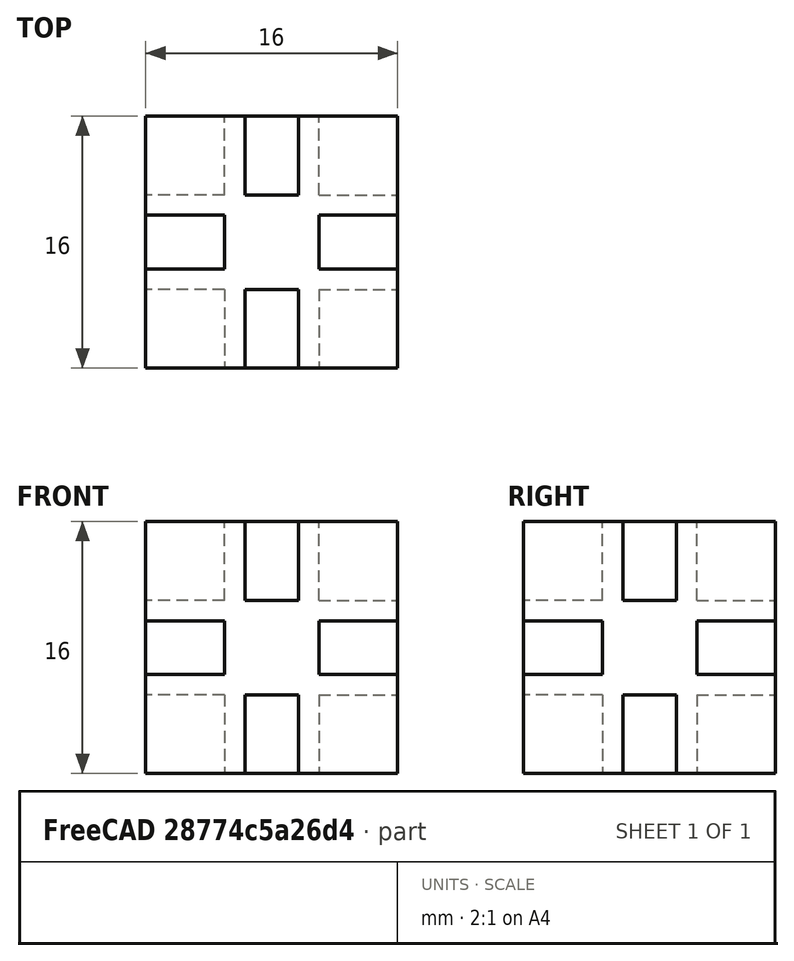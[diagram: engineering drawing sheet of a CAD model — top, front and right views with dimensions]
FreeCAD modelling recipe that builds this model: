
FCSTD DOCUMENT  (FreeCAD 0.14R3702 (Git))
Label: estanteria_disquette2
License: CC-BY 3.0
LicenseURL: http://creativecommons.org/licenses/by/3.0/
objects: Part::Box×2, Part::FeaturePython×2, Part::Cut×1
note: 5 computed .brp shape members not serialized (recipe doc carries the construction recipe); baked Part::Feature solids carry a one-line shape summary decoded from their .brp

FEATURE [Part::Box] Box002  label="Cubo002"
  Height = 3.4
  Length = 90
  Placement = pos=(3,3,-1.7) rot=(0,0,1;0rad)
  Width = 90
FEATURE [Part::FeaturePython] Array004  # Draft array (typed FeaturePython)
  Angle = 180
  ArrayType = 1
  Axis = (0,1,0)
  Base = -> Box002
  Center = (0,0,0)
  IntervalX = (1,0,0)
  IntervalY = (0,1,0)
  IntervalZ = (0,0,1)
  NumberPolar = 3
  NumberX = 1
  NumberY = 1
  NumberZ = 1
FEATURE [Part::FeaturePython] Array  # Draft array (typed FeaturePython)
  Angle = 360
  ArrayType = 1
  Axis = (1,0,0)
  Base = -> Array004
  Center = (0,0,0)
  IntervalX = (1,0,0)
  IntervalY = (0,1,0)
  IntervalZ = (0,0,1)
  NumberPolar = 4
  NumberX = 1
  NumberY = 1
  NumberZ = 1
FEATURE [Part::Box] Box  label="Cubo004"
  Height = 16
  Length = 16
  Placement = pos=(-8,-8,-8) rot=(0,0,1;0rad)
  Width = 16
FEATURE [Part::Cut] Cut001
  Base = -> Box
  Tool = -> Array
